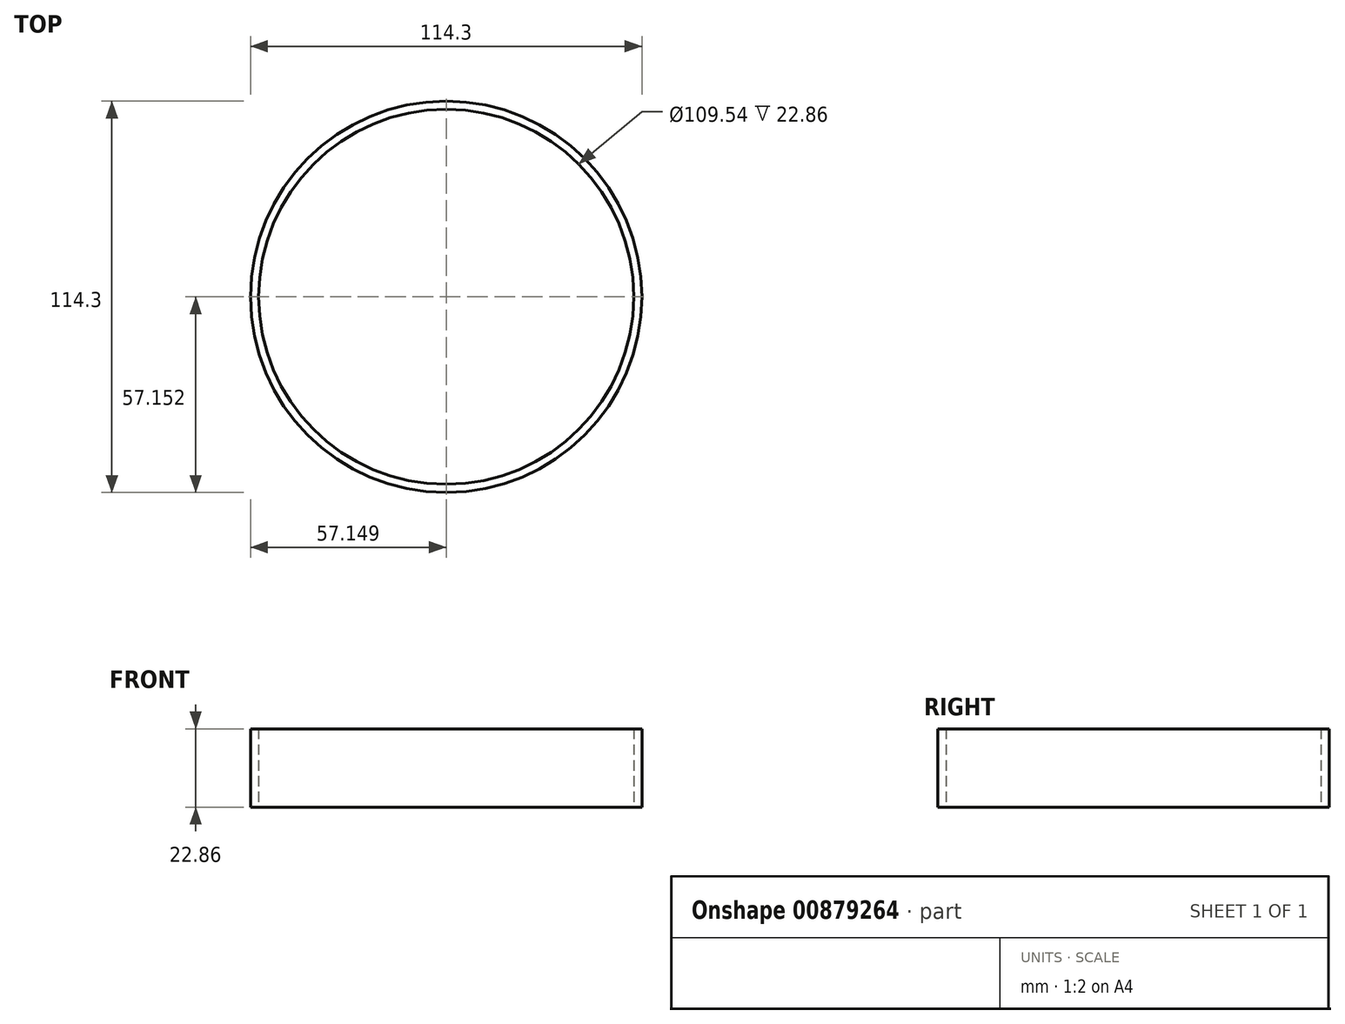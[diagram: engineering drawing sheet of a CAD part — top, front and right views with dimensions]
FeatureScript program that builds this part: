
annotation { "Feature Type Name" : "Feature", "Feature Type Description" : "" }
export const myFeature = defineFeature(function(context is Context, id is Id, definition is map)
    precondition{}
    {
        {
            var Q0;
            Q0=qCreatedBy(makeId("Top.planeOp"),FACE);
            var sketch = newSketch(context, id + "F0", { "sketchPlane" : qUnion([Q0])});
            skCircle(sketch, "E0", {"center": v(-42.01, 37.71) * mm, "radius": 38.1 * mm});
            skCircle(sketch, "E1", {"center": v(-42.01, 37.71) * mm, "radius": 36.51 * mm});
            skLineSegment(sketch, "E2", {"start": v(-42.01, 37.71) * mm, "end": v(-5.5, 37.71) * mm});
            skLineSegment(sketch, "E3.1.0", {"start": v(-42.01, 37.71) * mm, "end": v(-23.75, 69.33) * mm});
            skLineSegment(sketch, "E3.2.0", {"start": v(-42.01, 37.71) * mm, "end": v(-60.27, 69.33) * mm});
            skLineSegment(sketch, "E3.3.0", {"start": v(-42.01, 37.71) * mm, "end": v(-78.52, 37.71) * mm});
            skLineSegment(sketch, "E3.4.0", {"start": v(-42.01, 37.71) * mm, "end": v(-60.27, 6.1) * mm});
            skLineSegment(sketch, "E3.5.0", {"start": v(-42.01, 37.71) * mm, "end": v(-23.75, 6.1) * mm});
            skCircle(sketch, "E4", {"center": v(-42.01, 37.71) * mm, "radius": 34.93 * mm});
            skSolve(sketch);
        }
        {
            var Q0;
            Q0=makeQuery(id+"F0.imprint","IMPRINT",FACE,{"disambiguationData":[TD([[makeQuery(id+"F0.imprint","IMPRINT",EDGE,{"derivedFrom":sQuery(id+"F0.wireOp",EDGE,"E0")}),1.0]])]});
            extrude(context, id + "F1", {"entities" : qUnion([Q0]), "depth" : 15.24 * mm, "offsetDistance" : 25.4 * mm});
        }
        {
            var Q0;
            Q0=qCreatedBy(makeId("Top.planeOp"),FACE);
            var sketch = newSketch(context, id + "F2", { "sketchPlane" : qUnion([Q0])});
            skCircle(sketch, "E5", {"center": v(-42, 37.71) * mm, "radius": 34.93 * mm});
            skSolve(sketch);
        }
        {
            var Q0;
            Q0=makeQuery(id+"F1.opExtrude","SWEPT_BODY",BODY,{"disambiguationData":[OSD([sQuery(id+"F0.wireOp",EDGE,"E0"),sQuery(id+"F0.wireOp",EDGE,"E1")])]});
            var Q1;
            Q1=sQuery(id+"F2.wireOp",EDGE,"E5");
            var Q2;
            Q2=sQuery(id+"F2.wireOp",VERTEX,"E5.center");
            transform(context, id + "F3", {"entities" : qUnion([Q0]), "transformType" : TransformType.SCALE_UNIFORMLY, "scale" : 1.5, "scalePoint" : qUnion([Q2]), "makeCopy" : false});
        }
    });
